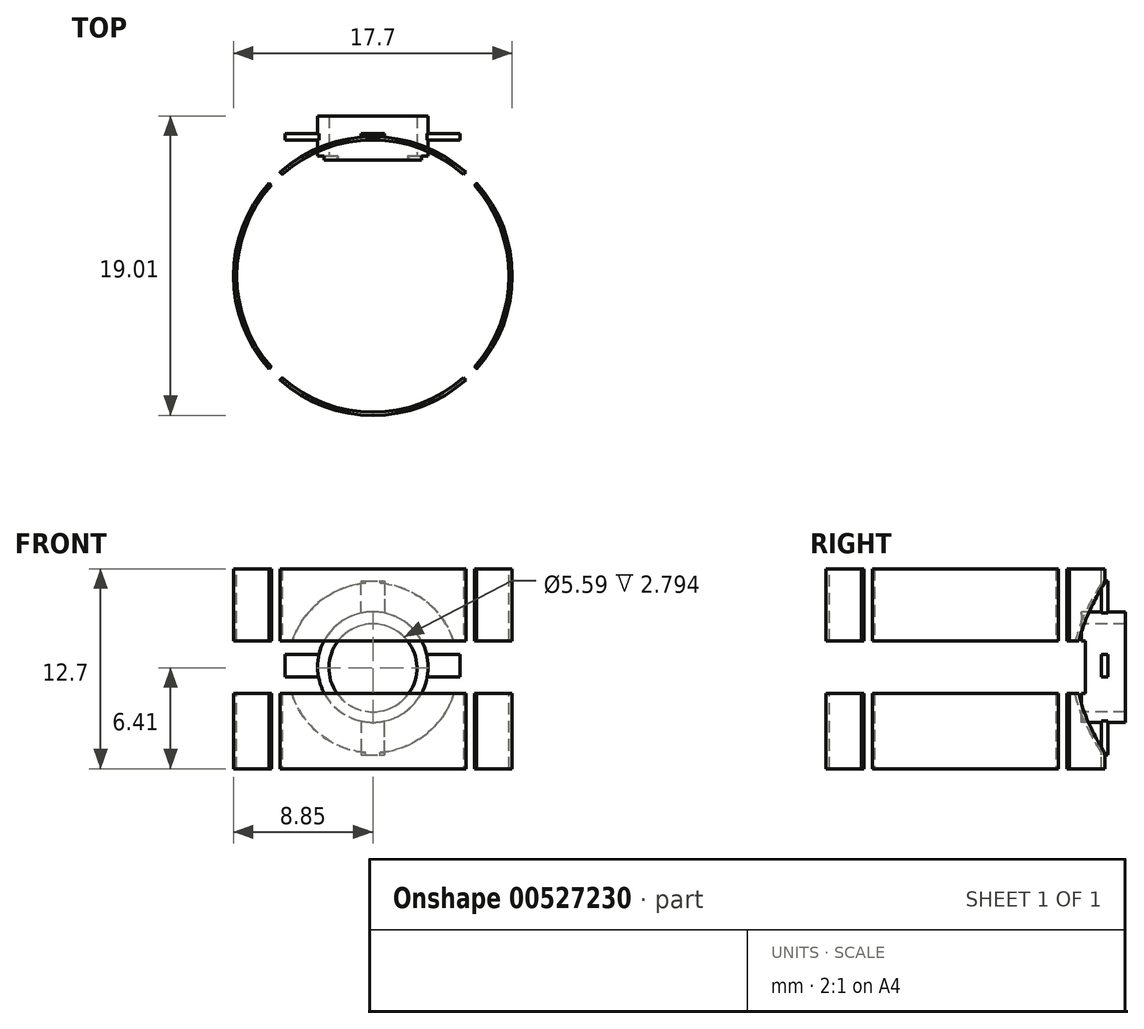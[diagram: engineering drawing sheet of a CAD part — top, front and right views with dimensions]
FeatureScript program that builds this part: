
annotation { "Feature Type Name" : "Feature", "Feature Type Description" : "" }
export const myFeature = defineFeature(function(context is Context, id is Id, definition is map)
    precondition{}
    {
        {
            var Q0;
            Q0=qCreatedBy(makeId("Top.planeOp"),FACE);
            var sketch = newSketch(context, id + "F0", { "sketchPlane" : qUnion([Q0])});
            skCircle(sketch, "E0", {"center": v(0, 0) * mm, "radius": 8.85 * mm});
            skSolve(sketch);
        }
        {
            var Q0;
            Q0=makeQuery(id+"F0.imprint","IMPRINT",FACE,{"disambiguationData":[TD([[makeQuery(id+"F0.imprint","IMPRINT",EDGE,{"derivedFrom":sQuery(id+"F0.wireOp",EDGE,"E0")}),1.0]])]});
            extrude(context, id + "F1", {"entities" : qUnion([Q0]), "depth" : 12.7 * mm, "offsetDistance" : 25.4 * mm});
        }
        {
            var Q0;
            Q0=makeQuery(id+"F1.opExtrude","CAP_FACE",FACE,{"disambiguationData":[OSD([sQuery(id+"F0.wireOp",EDGE,"E0")])],"isStart":false});
            var sketch = newSketch(context, id + "F2", { "sketchPlane" : qUnion([Q0])});
            skCircle(sketch, "E1.0", {"center": v(0, 0) * mm, "radius": 8.65 * mm});
            skLineSegment(sketch, "E2", {"start": v(-8.65, 0) * mm, "end": v(8.65, 0) * mm, "construction": true});
            skSolve(sketch);
        }
        {
            var Q0;
            Q0=makeQuery(id+"F2.imprint","IMPRINT",FACE,{"disambiguationData":[TD([[makeQuery(id+"F2.imprint","IMPRINT",EDGE,{"derivedFrom":sQuery(id+"F2.wireOp",EDGE,"E1.0")}),1.0]])]});
            extrude(context, id + "F3", {"entities" : qUnion([Q0]), "operationType" : NewBodyOperationType.REMOVE, "oppositeDirection" : true, "depth" : 25.4 * mm, "offsetDistance" : 25.4 * mm});
        }
        {
            var Q0;
            Q0=qCreatedBy(makeId("Front.planeOp"),FACE);
            var sketch = newSketch(context, id + "F4", { "sketchPlane" : qUnion([Q0])});
            skCircle(sketch, "E3", {"center": v(0, 6.41) * mm, "radius": 5.4 * mm});
            skSolve(sketch);
        }
        {
            var Q0;
            Q0 = qSketchRegion(id + "F4", true);
            extrude(context, id + "F5", {"entities" : qUnion([Q0]), "operationType" : NewBodyOperationType.REMOVE, "oppositeDirection" : true, "depth" : 25.4 * mm, "offsetDistance" : 25.4 * mm});
        }
        {
            var Q0;
            Q0=qCreatedBy(makeId("Front.planeOp"),FACE);
            var sketch = newSketch(context, id + "F6", { "sketchPlane" : qUnion([Q0])});
            skLineSegment(sketch, "E4", {"start": v(3.43, 7.27) * mm, "end": v(3.43, 5.83) * mm});
            skLineSegment(sketch, "E5", {"start": v(3.43, 5.83) * mm, "end": v(5.53, 5.83) * mm});
            skLineSegment(sketch, "E6", {"start": v(5.53, 5.83) * mm, "end": v(5.53, 7.27) * mm});
            skLineSegment(sketch, "E7", {"start": v(5.53, 7.27) * mm, "end": v(3.43, 7.27) * mm});
            skLineSegment(sketch, "E8", {"start": v(-3.29, 7.27) * mm, "end": v(-3.29, 5.83) * mm});
            skPoint(sketch, "E8.startSnap0", {"position": v(4.48, 7.27) * mm});
            skLineSegment(sketch, "E9", {"start": v(-3.29, 5.83) * mm, "end": v(-5.56, 5.83) * mm});
            skLineSegment(sketch, "E10", {"start": v(-5.56, 5.83) * mm, "end": v(-5.56, 7.27) * mm});
            skLineSegment(sketch, "E11", {"start": v(-5.56, 7.27) * mm, "end": v(-3.29, 7.27) * mm});
            skLineSegment(sketch, "E12", {"start": v(0.74, 9.82) * mm, "end": v(-0.76, 9.82) * mm});
            skLineSegment(sketch, "E13", {"start": v(-0.76, 9.82) * mm, "end": v(-0.76, 11.94) * mm});
            skLineSegment(sketch, "E14", {"start": v(-0.76, 11.94) * mm, "end": v(0.74, 11.94) * mm});
            skLineSegment(sketch, "E15", {"start": v(0.74, 11.94) * mm, "end": v(0.74, 9.82) * mm});
            skLineSegment(sketch, "E16", {"start": v(0.74, 3.16) * mm, "end": v(-0.76, 3.16) * mm});
            skLineSegment(sketch, "E17", {"start": v(-0.76, 3.16) * mm, "end": v(-0.76, 0.88) * mm});
            skLineSegment(sketch, "E18", {"start": v(-0.76, 0.88) * mm, "end": v(0.74, 0.88) * mm});
            skLineSegment(sketch, "E19", {"start": v(0.74, 0.88) * mm, "end": v(0.74, 3.16) * mm});
            skSolve(sketch);
        }
        {
            var Q0;
            Q0 = qSketchRegion(id + "F6", true);
            extrude(context, id + "F7", {"entities" : qUnion([Q0]), "operationType" : NewBodyOperationType.ADD, "oppositeDirection" : true, "depth" : 9.04 * mm, "offsetDistance" : 25.4 * mm, "hasSecondDirection" : true, "secondDirectionOppositeDirection" : true, "secondDirectionDepth" : 8.64 * mm});
        }
        {
            var Q0;
            Q0=qCreatedBy(makeId("Front.planeOp"),FACE);
            var sketch = newSketch(context, id + "F8", { "sketchPlane" : qUnion([Q0])});
            skCircle(sketch, "E20", {"center": v(0, 6.47) * mm, "radius": 3.51 * mm});
            skSolve(sketch);
        }
        {
            var Q0;
            Q0=makeQuery(id+"F8.imprint","IMPRINT",FACE,{"disambiguationData":[TD([[makeQuery(id+"F8.imprint","IMPRINT",EDGE,{"derivedFrom":sQuery(id+"F8.wireOp",EDGE,"E20")}),1.0]])]});
            extrude(context, id + "F9", {"entities" : qUnion([Q0]), "operationType" : NewBodyOperationType.ADD, "oppositeDirection" : true, "depth" : 10.16 * mm, "offsetDistance" : 25.4 * mm, "hasSecondDirection" : true, "secondDirectionOppositeDirection" : true, "secondDirectionDepth" : 7.37 * mm});
        }
        {
            var Q0;
            Q0=qCreatedBy(makeId("Front.planeOp"),FACE);
            var sketch = newSketch(context, id + "F10", { "sketchPlane" : qUnion([Q0])});
            skCircle(sketch, "E21", {"center": v(0, 6.41) * mm, "radius": 2.8 * mm});
            skSolve(sketch);
        }
        {
            var Q0;
            Q0=makeQuery(id+"F10.imprint","IMPRINT",FACE,{"disambiguationData":[TD([[makeQuery(id+"F10.imprint","IMPRINT",EDGE,{"derivedFrom":sQuery(id+"F10.wireOp",EDGE,"E21")}),1.0]])]});
            var Q1;
            Q1=makeQuery(id+"F9.opExtrude","CAP_FACE",FACE,{"disambiguationData":[OSD([sQuery(id+"F8.wireOp",EDGE,"E20")])],"isStart":false});
            extrude(context, id + "F11", {"entities" : qUnion([Q0]), "operationType" : NewBodyOperationType.REMOVE, "endBound" : BoundingType.UP_TO_SURFACE, "oppositeDirection" : true, "depth" : 17.78 * mm, "endBoundEntityFace" : qUnion([Q1]), "offsetDistance" : 25.4 * mm});
        }
        {
            var Q0;
            Q0=qCreatedBy(makeId("Front.planeOp"),FACE);
            var sketch = newSketch(context, id + "F12", { "sketchPlane" : qUnion([Q0])});
            skLineSegment(sketch, "E22", {"start": v(-14.57, 8.13) * mm, "end": v(13.89, 8.13) * mm});
            skLineSegment(sketch, "E23", {"start": v(13.89, 8.13) * mm, "end": v(13.89, 4.79) * mm});
            skLineSegment(sketch, "E24", {"start": v(13.89, 4.79) * mm, "end": v(-14.57, 4.79) * mm});
            skLineSegment(sketch, "E25", {"start": v(-14.57, 4.79) * mm, "end": v(-14.57, 8.13) * mm});
            skSolve(sketch);
        }
        {
            var Q0;
            Q0=makeQuery(id+"F12.imprint","IMPRINT",FACE,{"disambiguationData":[TD([[makeQuery(id+"F12.imprint","IMPRINT",EDGE,{"derivedFrom":sQuery(id+"F12.wireOp",EDGE,"E22")}),-1.0]])]});
            extrude(context, id + "F13", {"entities" : qUnion([Q0]), "operationType" : NewBodyOperationType.REMOVE, "depth" : 25.4 * mm, "offsetDistance" : 25.4 * mm, "hasSecondDirection" : true, "secondDirectionOppositeDirection" : true, "secondDirectionDepth" : 7.62 * mm});
        }
        {
            var Q0;
            Q0=qCreatedBy(makeId("Top.planeOp"),FACE);
            var sketch = newSketch(context, id + "F14", { "sketchPlane" : qUnion([Q0])});
            skCircle(sketch, "E26", {"center": v(6.19, 6.19) * mm, "radius": 0.5 * mm});
            skCircle(sketch, "E27", {"center": v(6.19, -6.19) * mm, "radius": 0.5 * mm});
            skCircle(sketch, "E28", {"center": v(-6.19, -6.19) * mm, "radius": 0.5 * mm});
            skCircle(sketch, "E29", {"center": v(-6.19, 6.19) * mm, "radius": 0.5 * mm});
            skLineSegment(sketch, "E30.bottom", {"start": v(-6.19, 6.19) * mm, "end": v(6.19, 6.19) * mm, "construction": true});
            skLineSegment(sketch, "E30.top", {"start": v(-6.19, -6.19) * mm, "end": v(6.19, -6.19) * mm, "construction": true});
            skLineSegment(sketch, "E30.left", {"start": v(-6.19, 6.19) * mm, "end": v(-6.19, -6.19) * mm, "construction": true});
            skLineSegment(sketch, "E30.right", {"start": v(6.19, 6.19) * mm, "end": v(6.19, -6.19) * mm, "construction": true});
            skLineSegment(sketch, "E31", {"start": v(-6.19, 6.19) * mm, "end": v(6.19, -6.19) * mm, "construction": true});
            skLineSegment(sketch, "E32", {"start": v(6.19, 6.19) * mm, "end": v(-6.19, -6.19) * mm, "construction": true});
            skPoint(sketch, "E33", {"position": v(0, 0) * mm});
            skCircle(sketch, "E34.0", {"center": v(0, 0) * mm, "radius": 8.85 * mm, "construction": true});
            skCircle(sketch, "E35.0", {"center": v(0, 0) * mm, "radius": 8.65 * mm, "construction": true});
            skLineSegment(sketch, "E36", {"start": v(0, -8.85) * mm, "end": v(0, -8.65) * mm, "construction": true});
            skPoint(sketch, "E37", {"position": v(0, -6.19) * mm});
            skCircle(sketch, "E38", {"center": v(0, 0) * mm, "radius": 8.75 * mm, "construction": true});
            skPoint(sketch, "E39", {"position": v(0, -8.75) * mm});
            skSolve(sketch);
        }
        {
            var Q0;
            Q0 = qSketchRegion(id + "F14", true);
            extrude(context, id + "F15", {"entities" : qUnion([Q0]), "operationType" : NewBodyOperationType.REMOVE, "depth" : 40.13 * mm, "offsetDistance" : 25.4 * mm});
        }
    });
